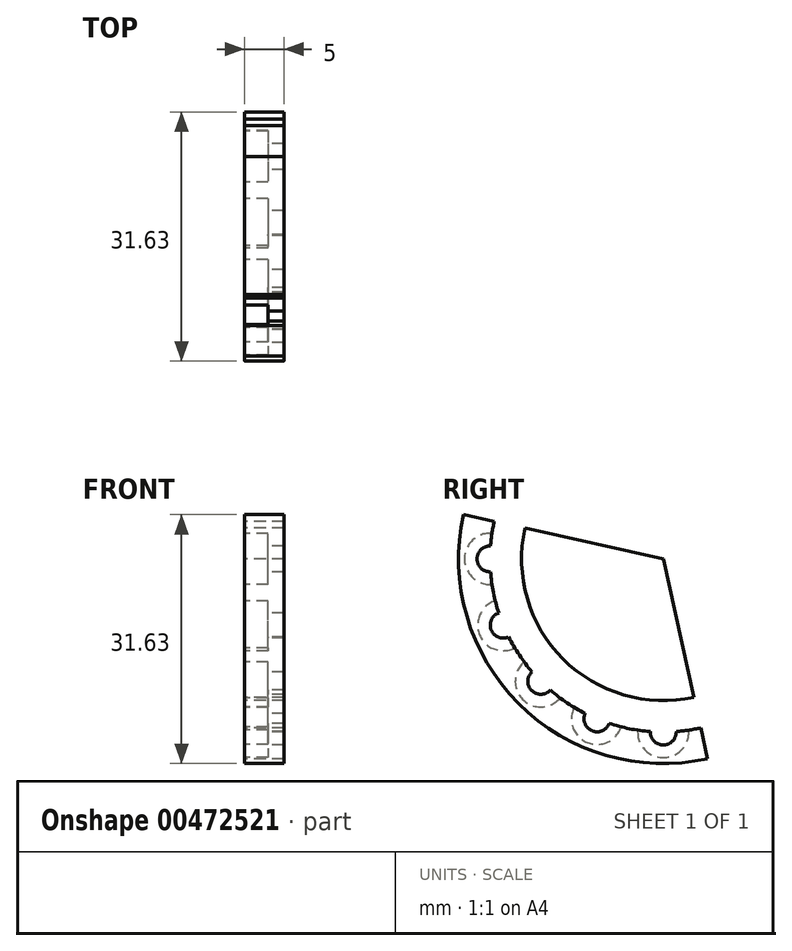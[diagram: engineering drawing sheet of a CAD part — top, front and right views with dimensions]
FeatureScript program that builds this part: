
annotation { "Feature Type Name" : "Feature", "Feature Type Description" : "" }
export const myFeature = defineFeature(function(context is Context, id is Id, definition is map)
    precondition{}
    {
        {
            var Q0;
            Q0=qCreatedBy(makeId("Right.planeOp"),FACE);
            var sketch = newSketch(context, id + "F0", { "sketchPlane" : qUnion([Q0])});
            skArc(sketch, "E0", {"start": v(-25.38, 5.63) * mm, "mid": v(-18.38, -18.38) * mm, "end": v(5.63, -25.38) * mm});
            skLineSegment(sketch, "E1", {"start": v(0, 0) * mm, "end": v(5.63, -25.38) * mm});
            skLineSegment(sketch, "E2", {"start": v(0, 0) * mm, "end": v(-25.38, 5.63) * mm});
            skArc(sketch, "E3", {"start": v(-21.48, 4.76) * mm, "mid": v(-15.56, -15.56) * mm, "end": v(4.76, -21.48) * mm});
            skPoint(sketch, "E4", {"position": v(-22, 0) * mm});
            skPoint(sketch, "E5", {"position": v(0, -22) * mm});
            skArc(sketch, "E6", {"start": v(-22, 0) * mm, "mid": v(-20.33, -8.42) * mm, "end": v(-15.56, -15.56) * mm});
            skArc(sketch, "E7", {"start": v(-22, 0) * mm, "mid": v(-21.58, -4.3) * mm, "end": v(-20.33, -8.42) * mm});
            skArc(sketch, "E8", {"start": v(-15.56, -15.56) * mm, "mid": v(-8.42, -20.33) * mm, "end": v(0, -22) * mm});
            skArc(sketch, "E9", {"start": v(-15.56, -15.56) * mm, "mid": v(-12.22, -18.3) * mm, "end": v(-8.42, -20.33) * mm});
            skArc(sketch, "E10", {"start": v(-17.57, 3.9) * mm, "mid": v(-12.73, -12.73) * mm, "end": v(3.9, -17.57) * mm});
            skArc(sketch, "E11", {"start": v(-3.9, 0.87) * mm, "mid": v(2.83, 2.83) * mm, "end": v(0.87, -3.9) * mm});
            skLineSegment(sketch, "E12", {"start": v(0, 0) * mm, "end": v(-15.56, -15.56) * mm, "construction": true});
            skLineSegment(sketch, "E13", {"start": v(0, 0) * mm, "end": v(-31.17, 0) * mm, "construction": true});
            skLineSegment(sketch, "E14", {"start": v(-20.33, -8.42) * mm, "end": v(0, 0) * mm, "construction": true});
            skLineSegment(sketch, "E15", {"start": v(-8.42, -20.33) * mm, "end": v(0, 0) * mm, "construction": true});
            skLineSegment(sketch, "E16", {"start": v(0, -22) * mm, "end": v(0, 0) * mm, "construction": true});
            skSolve(sketch);
        }
        {
            var Q0;
            {var subQ4=sQuery(id+"F0.wireOp",EDGE,"E0");Q0=makeQuery(id+"F0.imprint","IMPRINT",FACE,{"disambiguationData":[TD([[makeQuery(id+"F0.imprint","IMPRINT",EDGE,{"derivedFrom":subQ4}),1.0]])]});}
            var Q1;
            Q1=makeQuery(id+"F0.imprint","IMPRINT",FACE,{"disambiguationData":[TD([[makeQuery(id+"F0.imprint","IMPRINT",EDGE,{"derivedFrom":sQuery(id+"F0.wireOp",EDGE,"E6")}),1.0]])]});
            var Q2;
            {var subQ0=sQuery(id+"F0.wireOp",EDGE,"E10");Q2=makeQuery(id+"F0.imprint","IMPRINT",FACE,{"disambiguationData":[TD([[makeQuery(id+"F0.imprint","IMPRINT",EDGE,{"derivedFrom":subQ0}),1.0]])]});}
            var Q3;
            {var subQ3=sQuery(id+"F0.wireOp",EDGE,"E11");Q3=makeQuery(id+"F0.imprint","IMPRINT",FACE,{"disambiguationData":[TD([[makeQuery(id+"F0.imprint","IMPRINT",EDGE,{"derivedFrom":subQ3}),-1.0]])]});}
            extrude(context, id + "F1", {"entities" : qUnion([Q0, Q1, Q2, Q3]), "depth" : 5 * mm});
        }
        {
            var Q0;
            Q0=sQuery(id+"F0.wireOp",VERTEX,"E4");
            var Q1;
            Q1=sQuery(id+"F0.wireOp",VERTEX,"E7.end");
            var Q2;
            Q2=sQuery(id+"F0.wireOp",VERTEX,"E9.start");
            var Q3;
            Q3=sQuery(id+"F0.wireOp",VERTEX,"E9.end");
            var Q4;
            Q4=sQuery(id+"F0.wireOp",VERTEX,"E5");
            var Q5;
            Q5=sQuery(id+"F0.wireOp",VERTEX,"E7.center");
            var Q6;
            Q6=makeQuery(id+"F1.opExtrude","SWEPT_BODY",BODY,{"disambiguationData":[OSD([sQuery(id+"F0.wireOp",EDGE,"E0"),sQuery(id+"F0.wireOp",EDGE,"E1"),sQuery(id+"F0.wireOp",EDGE,"E2")])]});
            hole(context, id + "F2", {"style" : HoleStyle.C_BORE, "endStyle" : HoleEndStyle.THROUGH, "oppositeDirection" : true, "standardTappedOrClearance" : lookupTablePath({ "standard" : "ISO", "fit" : "Normal", "size" : "M3", "type" : "Clearance" }), "standardBlindInLast" : lookupTablePath({ "fit" : "Standard", "standard" : "ISO", "size" : "M3", "type" : "Clearance" }), "holeDiameter" : 3.3 * mm, "cBoreDiameter" : 6.5 * mm, "cBoreDepth" : 3 * mm, "majorDiameter" : 5 * mm, "locations" : qUnion([Q0, Q1, Q2, Q3, Q4, Q5]), "scope" : qUnion([Q6]), "isTappedThrough" : true, "tappedDepth" : 12 * mm, "tapClearance" : 3});
        }
    });
